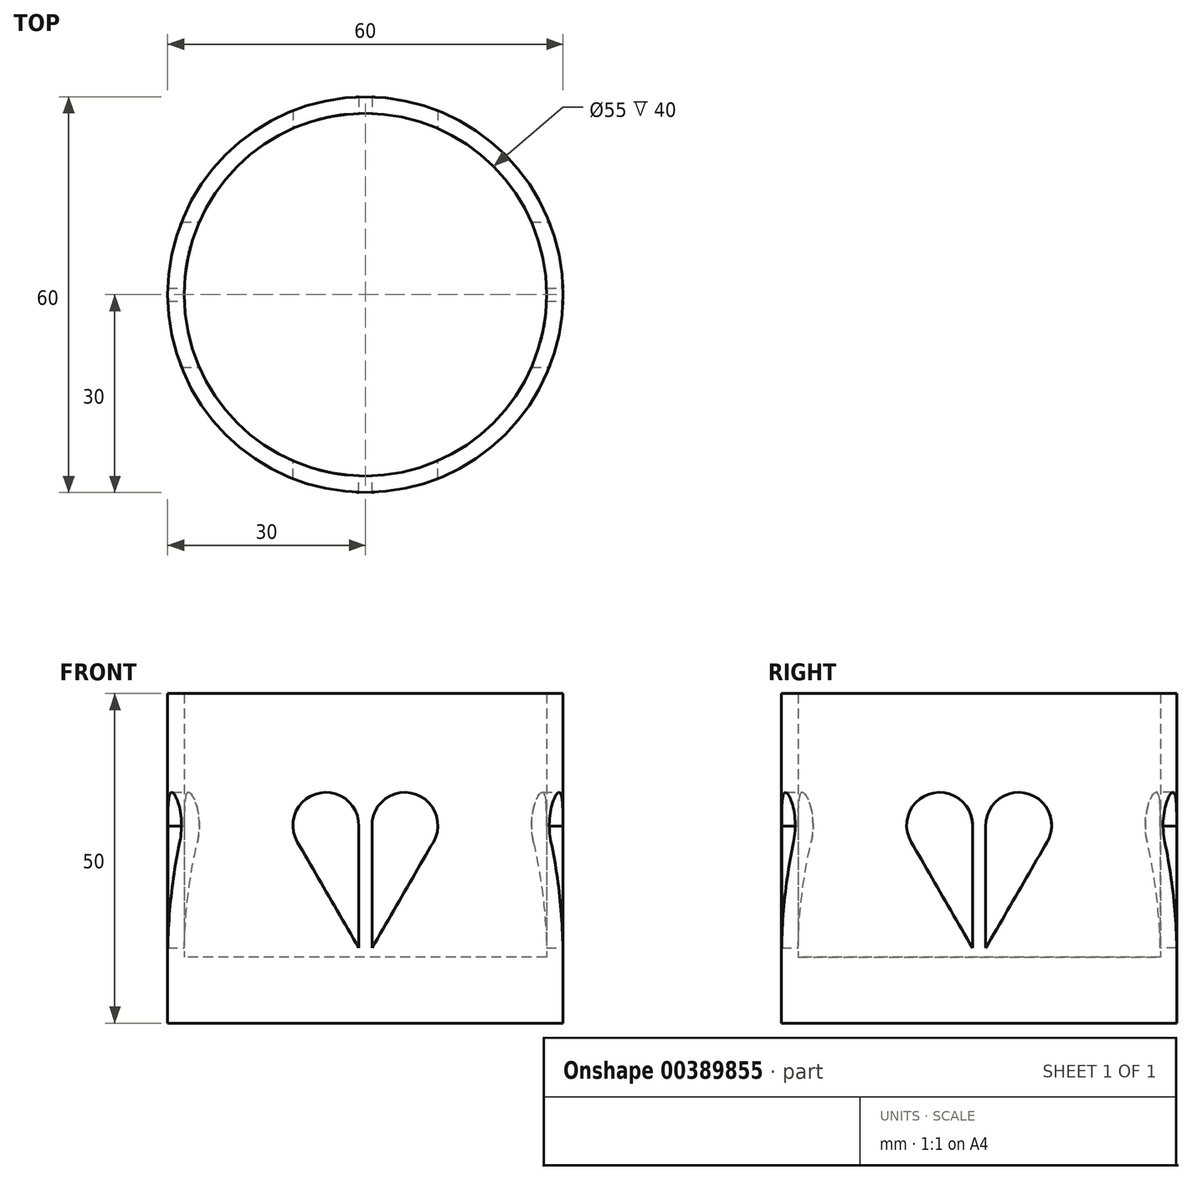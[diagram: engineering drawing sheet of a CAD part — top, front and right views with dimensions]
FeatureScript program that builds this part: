
annotation { "Feature Type Name" : "Feature", "Feature Type Description" : "" }
export const myFeature = defineFeature(function(context is Context, id is Id, definition is map)
    precondition{}
    {
        {
            var Q0;
            Q0=qCreatedBy(makeId("Top.planeOp"),FACE);
            var sketch = newSketch(context, id + "F0", { "sketchPlane" : qUnion([Q0])});
            skCircle(sketch, "E0", {"center": v(0, 0) * mm, "radius": 30 * mm});
            skSolve(sketch);
        }
        {
            var Q0;
            Q0=makeQuery(id+"F0.imprint","IMPRINT",FACE,{"disambiguationData":[TD([[makeQuery(id+"F0.imprint","IMPRINT",EDGE,{"derivedFrom":sQuery(id+"F0.wireOp",EDGE,"E0")}),1.0]])]});
            extrude(context, id + "F1", {"entities" : qUnion([Q0]), "depth" : 10 * mm});
        }
        {
            var Q0;
            Q0=makeQuery(id+"F1.opExtrude","CAP_FACE",FACE,{"disambiguationData":[OSD([sQuery(id+"F0.wireOp",EDGE,"E0")])],"isStart":false});
            var sketch = newSketch(context, id + "F2", { "sketchPlane" : qUnion([Q0])});
            skCircle(sketch, "E1", {"center": v(0, 0) * mm, "radius": 30 * mm});
            skCircle(sketch, "E2", {"center": v(0, 0) * mm, "radius": 27.5 * mm});
            skSolve(sketch);
        }
        {
            var Q0;
            Q0=makeQuery(id+"F2.imprint","IMPRINT",FACE,{"disambiguationData":[TD([[makeQuery(id+"F2.imprint","IMPRINT",EDGE,{"derivedFrom":sQuery(id+"F2.wireOp",EDGE,"E1")}),1.0]])]});
            extrude(context, id + "F3", {"entities" : qUnion([Q0]), "operationType" : NewBodyOperationType.ADD, "depth" : 40 * mm});
        }
        {
            var Q0;
            Q0=qCreatedBy(makeId("Front.planeOp"),FACE);
            var sketch = newSketch(context, id + "F4", { "sketchPlane" : qUnion([Q0])});
            skCircle(sketch, "E3", {"center": v(6, 30) * mm, "radius": 5 * mm});
            skCircle(sketch, "E4", {"center": v(-6, 30) * mm, "radius": 5 * mm});
            skLineSegment(sketch, "E5", {"start": v(-1, 29.85) * mm, "end": v(-1, 11.4) * mm});
            skLineSegment(sketch, "E6", {"start": v(-1, 11.4) * mm, "end": v(-10.33, 27.5) * mm});
            skLineSegment(sketch, "E7", {"start": v(-10.33, 27.5) * mm, "end": v(-1, 29.85) * mm});
            skLineSegment(sketch, "E8.MirrorCS", {"start": v(1, 11.4) * mm, "end": v(10.33, 27.5) * mm});
            skLineSegment(sketch, "E9.MirrorCS", {"start": v(10.33, 27.5) * mm, "end": v(1, 29.85) * mm});
            skLineSegment(sketch, "E10.MirrorCS", {"start": v(1, 29.85) * mm, "end": v(1, 11.4) * mm});
            skSolve(sketch);
        }
        {
            var Q0;
            {var subQ0=sQuery(id+"F4.wireOp",EDGE,"E7");Q0=makeQuery(id+"F4.imprint","IMPRINT",FACE,{"disambiguationData":[TD([[makeQuery(id+"F4.imprint","IMPRINT",EDGE,{"derivedFrom":subQ0}),1.0]])]});}
            var Q1;
            {var subQ0=sQuery(id+"F4.wireOp",EDGE,"E7");Q1=makeQuery(id+"F4.imprint","IMPRINT",FACE,{"disambiguationData":[TD([[makeQuery(id+"F4.imprint","IMPRINT",EDGE,{"derivedFrom":subQ0}),-1.0]])]});}
            var Q2;
            {var subQ1=sQuery(id+"F4.wireOp",EDGE,"E5");Q2=makeQuery(id+"F4.imprint","IMPRINT",FACE,{"disambiguationData":[TD([[makeQuery(id+"F4.imprint","IMPRINT",EDGE,{"derivedFrom":subQ1}),-1.0]])]});}
            var Q3;
            {var subQ0=sQuery(id+"F4.wireOp",EDGE,"E9.MirrorCS");Q3=makeQuery(id+"F4.imprint","IMPRINT",FACE,{"disambiguationData":[TD([[makeQuery(id+"F4.imprint","IMPRINT",EDGE,{"derivedFrom":subQ0}),-1.0]])]});}
            var Q4;
            {var subQ0=sQuery(id+"F4.wireOp",EDGE,"E9.MirrorCS");Q4=makeQuery(id+"F4.imprint","IMPRINT",FACE,{"disambiguationData":[TD([[makeQuery(id+"F4.imprint","IMPRINT",EDGE,{"derivedFrom":subQ0}),1.0]])]});}
            var Q5;
            {var subQ1=sQuery(id+"F4.wireOp",EDGE,"E8.MirrorCS");Q5=makeQuery(id+"F4.imprint","IMPRINT",FACE,{"disambiguationData":[TD([[makeQuery(id+"F4.imprint","IMPRINT",EDGE,{"derivedFrom":subQ1}),1.0]])]});}
            extrude(context, id + "F5", {"entities" : qUnion([Q0, Q1, Q2, Q3, Q4, Q5]), "operationType" : NewBodyOperationType.REMOVE, "oppositeDirection" : true, "depth" : 35 * mm});
        }
        {
            var Q0;
            Q0 = qSketchRegion(id + "F4", true);
            extrude(context, id + "F6", {"entities" : qUnion([Q0]), "operationType" : NewBodyOperationType.REMOVE, "oppositeDirection" : true, "depth" : -35 * mm});
        }
        {
            var Q0;
            Q0 = qSketchRegion(id + "F4", true);
            extrude(context, id + "F7", {"entities" : qUnion([Q0]), "depth" : 0 * mm});
        }
        {
            var Q0;
            Q0=makeQuery(id+"F7.opExtrude","SWEPT_BODY",BODY,{"disambiguationData":[OSD([sQuery(id+"F4.wireOp",EDGE,"E4"),sQuery(id+"F4.wireOp",EDGE,"E5"),sQuery(id+"F4.wireOp",EDGE,"E6")])]});
            var Q1;
            Q1=makeQuery(id+"F7.opExtrude","SWEPT_BODY",BODY,{"disambiguationData":[OSD([sQuery(id+"F4.wireOp",EDGE,"E3"),sQuery(id+"F4.wireOp",EDGE,"E8.MirrorCS"),sQuery(id+"F4.wireOp",EDGE,"E10.MirrorCS")])]});
            var Q2;
            Q2=makeQuery(id+"F3.boolean.opBoolean","MERGE",FACE,{"derivedFrom":[makeQuery(id+"F1.opExtrude","SWEPT_FACE",FACE,{"disambiguationData":[OSD([sQuery(id+"F0.wireOp",EDGE,"E0")])]}),makeQuery(id+"F3.opExtrude","SWEPT_FACE",FACE,{"disambiguationData":[OSD([sQuery(id+"F2.wireOp",EDGE,"E1")])]})]});
            transform(context, id + "F8", {"entities" : qUnion([Q0, Q1]), "transformType" : TransformType.ROTATION, "transformAxis" : qUnion([Q2]), "angle" : 90 * degree, "makeCopy" : false});
        }
        {
            var Q0;
            Q0=makeQuery(id+"F7.opExtrude","SWEPT_BODY",BODY,{"disambiguationData":[OSD([sQuery(id+"F4.wireOp",EDGE,"E3"),sQuery(id+"F4.wireOp",EDGE,"E8.MirrorCS"),sQuery(id+"F4.wireOp",EDGE,"E10.MirrorCS")])]});
            var Q1;
            Q1=makeQuery(id+"F7.opExtrude","SWEPT_BODY",BODY,{"disambiguationData":[OSD([sQuery(id+"F4.wireOp",EDGE,"E4"),sQuery(id+"F4.wireOp",EDGE,"E5"),sQuery(id+"F4.wireOp",EDGE,"E6")])]});
            transform(context, id + "F9", {"entities" : qUnion([Q0, Q1]), "transformType" : TransformType.TRANSLATION_3D, "dx" : 48.6 * mm, "dy" : 0 * mm, "dz" : 0 * mm, "makeCopy" : false});
        }
        {
            var Q0;
            Q0=makeQuery(id+"F7.opExtrude","CAP_FACE",FACE,{"disambiguationData":[OSD([sQuery(id+"F4.wireOp",EDGE,"E3"),sQuery(id+"F4.wireOp",EDGE,"E8.MirrorCS"),sQuery(id+"F4.wireOp",EDGE,"E10.MirrorCS")])],"isStart":true});
            var Q1;
            Q1=makeQuery(id+"F7.opExtrude","CAP_FACE",FACE,{"disambiguationData":[OSD([sQuery(id+"F4.wireOp",EDGE,"E4"),sQuery(id+"F4.wireOp",EDGE,"E5"),sQuery(id+"F4.wireOp",EDGE,"E6")])],"isStart":true});
            extrude(context, id + "F10", {"entities" : qUnion([Q0, Q1]), "operationType" : NewBodyOperationType.REMOVE, "oppositeDirection" : true, "depth" : 100 * mm});
        }
    });
